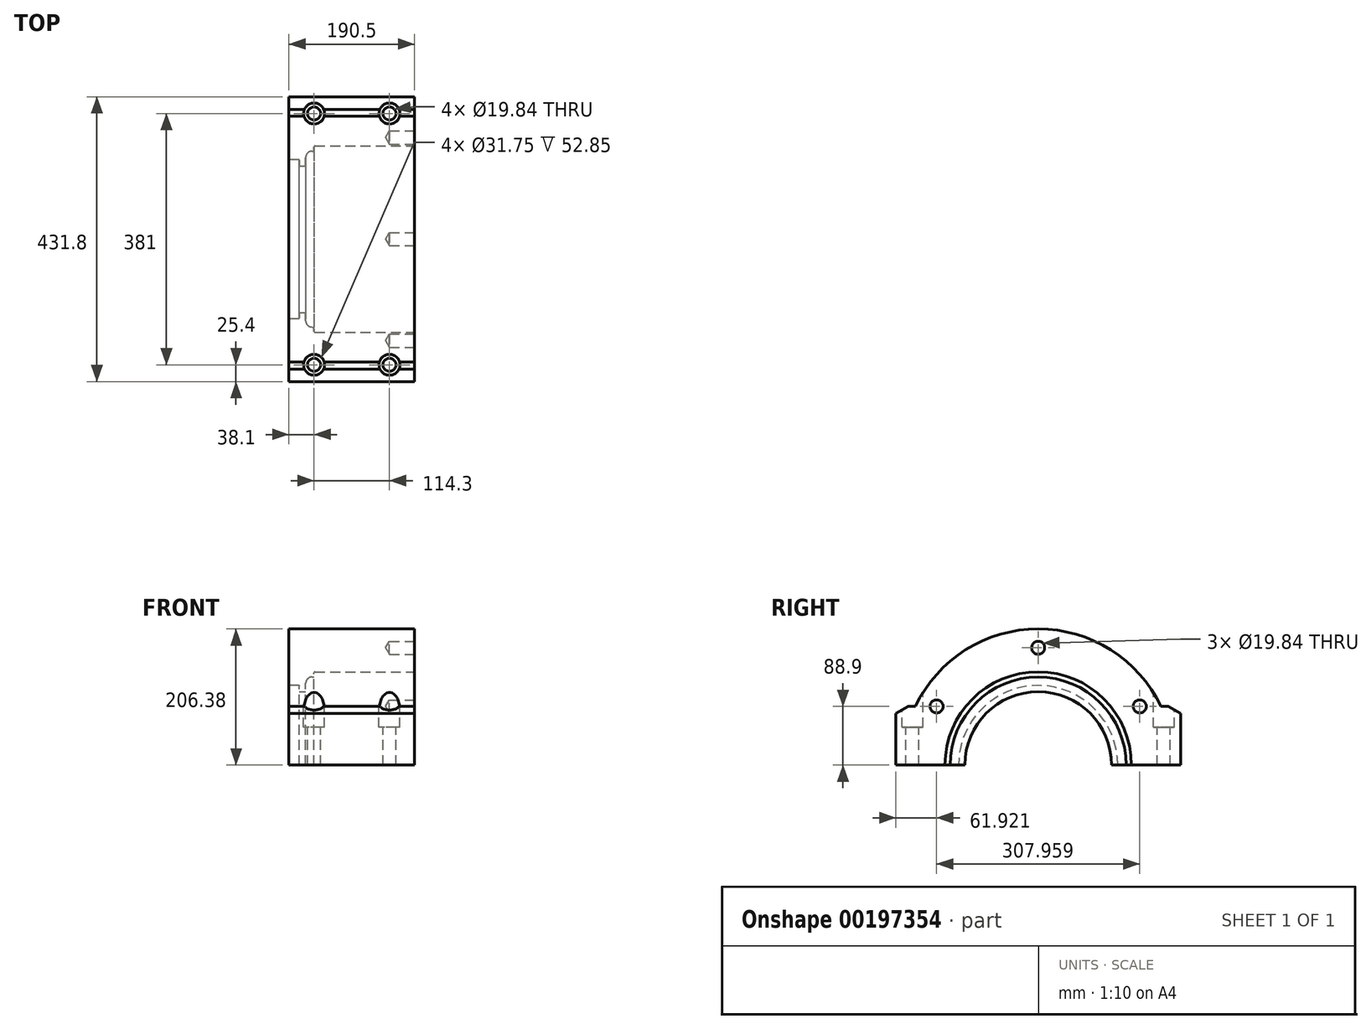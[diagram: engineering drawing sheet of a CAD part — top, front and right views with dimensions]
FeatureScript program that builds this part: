
annotation { "Feature Type Name" : "Feature", "Feature Type Description" : "" }
export const myFeature = defineFeature(function(context is Context, id is Id, definition is map)
    precondition{}
    {
        {
            var Q0;
            Q0=qCreatedBy(makeId("Right.planeOp"),FACE);
            var sketch = newSketch(context, id + "F0", { "sketchPlane" : qUnion([Q0])});
            skArc(sketch, "E0", {"start": v(186.25, 88.9) * mm, "mid": v(0, 206.38) * mm, "end": v(-186.25, 88.9) * mm});
            skLineSegment(sketch, "E1", {"start": v(-206.38, 0) * mm, "end": v(206.38, 0) * mm});
            skLineSegment(sketch, "E2", {"start": v(0, 324.9) * mm, "end": v(0, -120.15) * mm, "construction": true});
            skLineSegment(sketch, "E3.0", {"start": v(-215.9, 324.9) * mm, "end": v(-215.9, 88.9) * mm, "construction": true});
            skLineSegment(sketch, "E4", {"start": v(-330.26, 0) * mm, "end": v(259.86, 0) * mm, "construction": true});
            skLineSegment(sketch, "E5.0", {"start": v(-330.26, 88.9) * mm, "end": v(-215.9, 88.9) * mm, "construction": true});
            skLineSegment(sketch, "E6.bottom", {"start": v(-196.85, 88.9) * mm, "end": v(-166.34, 88.9) * mm});
            skLineSegment(sketch, "E6.top", {"start": v(-215.9, 0) * mm, "end": v(-166.34, 0) * mm});
            skLineSegment(sketch, "E6.left", {"start": v(-215.9, 77.9) * mm, "end": v(-215.9, 0) * mm});
            skLineSegment(sketch, "E7.0", {"start": v(-196.85, 324.9) * mm, "end": v(-196.85, 88.9) * mm, "construction": true});
            skLineSegment(sketch, "E8", {"start": v(-196.85, 88.9) * mm, "end": v(-215.9, 77.9) * mm});
            skLineSegment(sketch, "E9.trimOffspring", {"start": v(-196.85, 88.9) * mm, "end": v(-186.25, 88.9) * mm, "construction": true});
            skLineSegment(sketch, "E10.trimOffspring", {"start": v(-215.9, 77.9) * mm, "end": v(-215.9, -120.15) * mm, "construction": true});
            skLineSegment(sketch, "E11.trimOffspring", {"start": v(-166.34, 88.9) * mm, "end": v(259.86, 88.9) * mm, "construction": true});
            skLineSegment(sketch, "E12.MirrorCS", {"start": v(196.85, 88.9) * mm, "end": v(215.9, 77.9) * mm});
            skLineSegment(sketch, "E13.MirrorCS", {"start": v(196.85, 88.9) * mm, "end": v(186.25, 88.9) * mm, "construction": true});
            skLineSegment(sketch, "E14.MirrorCS", {"start": v(196.85, 88.9) * mm, "end": v(166.34, 88.9) * mm});
            skLineSegment(sketch, "E15.MirrorCS", {"start": v(215.9, 77.9) * mm, "end": v(215.9, 0) * mm});
            skLineSegment(sketch, "E16.MirrorCS", {"start": v(215.9, 0) * mm, "end": v(166.34, 0) * mm});
            skLineSegment(sketch, "E17.trimOffspring", {"start": v(-196.85, 0) * mm, "end": v(-196.85, -120.15) * mm, "construction": true});
            skSolve(sketch);
        }
        {
            var Q0;
            Q0 = qSketchRegion(id + "F0", true);
            extrude(context, id + "F1", {"entities" : qUnion([Q0]), "depth" : 190.5 * mm});
        }
        {
            var Q0;
            Q0=makeQuery(id+"F1.opExtrude","CAP_FACE",FACE,{"disambiguationData":[OSD([sQuery(id+"F0.wireOp",EDGE,"E0"),sQuery(id+"F0.wireOp",EDGE,"E1"),sQuery(id+"F0.wireOp",EDGE,"E6.bottom"),sQuery(id+"F0.wireOp",EDGE,"E6.top"),sQuery(id+"F0.wireOp",EDGE,"E6.left"),sQuery(id+"F0.wireOp",EDGE,"E8"),sQuery(id+"F0.wireOp",EDGE,"E12.MirrorCS"),sQuery(id+"F0.wireOp",EDGE,"E14.MirrorCS"),sQuery(id+"F0.wireOp",EDGE,"E15.MirrorCS"),sQuery(id+"F0.wireOp",EDGE,"E16.MirrorCS")])],"isStart":false});
            var sketch = newSketch(context, id + "F2", { "sketchPlane" : qUnion([Q0])});
            skCircle(sketch, "E18", {"center": v(0, 0) * mm, "radius": 141.29 * mm});
            skSolve(sketch);
        }
        {
            var Q0;
            Q0 = qSketchRegion(id + "F2", true);
            extrude(context, id + "F3", {"entities" : qUnion([Q0]), "operationType" : NewBodyOperationType.REMOVE, "oppositeDirection" : true, "depth" : 152.4 * mm});
        }
        {
            var Q0;
            Q0=makeQuery(id+"F3.boolean.opBoolean","COPY",FACE,{"derivedFrom":makeQuery(id+"F3.opExtrude","CAP_FACE",FACE,{"disambiguationData":[OSD([sQuery(id+"F2.wireOp",EDGE,"E18")])],"isStart":false})});
            var sketch = newSketch(context, id + "F4", { "sketchPlane" : qUnion([Q0])});
            skCircle(sketch, "E19", {"center": v(0, 0) * mm, "radius": 133.35 * mm});
            skSolve(sketch);
        }
        {
            var Q0;
            Q0 = qSketchRegion(id + "F4", true);
            extrude(context, id + "F5", {"entities" : qUnion([Q0]), "operationType" : NewBodyOperationType.REMOVE, "oppositeDirection" : true, "depth" : 12.7 * mm});
        }
        {
            var Q0;
            Q0=makeQuery(id+"F5.boolean.opBoolean","COPY",FACE,{"derivedFrom":makeQuery(id+"F5.opExtrude","CAP_FACE",FACE,{"disambiguationData":[OSD([sQuery(id+"F4.wireOp",EDGE,"E19")])],"isStart":false})});
            var sketch = newSketch(context, id + "F6", { "sketchPlane" : qUnion([Q0])});
            skCircle(sketch, "E20", {"center": v(0, 0) * mm, "radius": 111.13 * mm});
            skSolve(sketch);
        }
        {
            var Q0;
            Q0 = qSketchRegion(id + "F6", true);
            extrude(context, id + "F7", {"entities" : qUnion([Q0]), "operationType" : NewBodyOperationType.REMOVE, "endBound" : BoundingType.THROUGH_ALL, "oppositeDirection" : true, "depth" : 25.4 * mm});
        }
        {
            var Q0;
            Q0=makeQuery(id+"F3.boolean.opBoolean","COPY",EDGE,{"derivedFrom":makeQuery(id+"F3.opExtrude","CAP_EDGE",EDGE,{"disambiguationData":[OSD([sQuery(id+"F2.wireOp",EDGE,"E18")])],"isStart":false})});
            fillet(context, id + "F8", {"entities" : qUnion([Q0]), "radius" : 1.52 * mm, "tangentPropagation" : true, "allowEdgeOverflow" : false});
        }
        {
            var Q0;
            Q0=makeQuery(id+"F5.boolean.opBoolean","COPY",EDGE,{"derivedFrom":makeQuery(id+"F5.opExtrude","CAP_EDGE",EDGE,{"disambiguationData":[OSD([sQuery(id+"F4.wireOp",EDGE,"E19")])],"isStart":false})});
            fillet(context, id + "F9", {"entities" : qUnion([Q0]), "radius" : 9.65 * mm, "tangentPropagation" : true, "allowEdgeOverflow" : false});
        }
        {
            var Q0;
            Q0=makeQuery(id+"F1.opExtrude","CAP_FACE",FACE,{"disambiguationData":[OSD([sQuery(id+"F0.wireOp",EDGE,"E0"),sQuery(id+"F0.wireOp",EDGE,"E1"),sQuery(id+"F0.wireOp",EDGE,"E6.bottom"),sQuery(id+"F0.wireOp",EDGE,"E6.top"),sQuery(id+"F0.wireOp",EDGE,"E6.left"),sQuery(id+"F0.wireOp",EDGE,"E8"),sQuery(id+"F0.wireOp",EDGE,"E12.MirrorCS"),sQuery(id+"F0.wireOp",EDGE,"E14.MirrorCS"),sQuery(id+"F0.wireOp",EDGE,"E15.MirrorCS"),sQuery(id+"F0.wireOp",EDGE,"E16.MirrorCS")])],"isStart":true});
            var sketch = newSketch(context, id + "F10", { "sketchPlane" : qUnion([Q0])});
            skCircle(sketch, "E21", {"center": v(0, 0) * mm, "radius": 120.65 * mm});
            skSolve(sketch);
        }
        {
            var Q0;
            Q0 = qSketchRegion(id + "F10", true);
            extrude(context, id + "F11", {"entities" : qUnion([Q0]), "operationType" : NewBodyOperationType.REMOVE, "oppositeDirection" : true, "depth" : 15.75 * mm});
        }
        {
            var Q0;
            Q0=makeQuery(id+"F11.boolean.opBoolean","COPY",EDGE,{"derivedFrom":makeQuery(id+"F11.opExtrude","CAP_EDGE",EDGE,{"disambiguationData":[OSD([sQuery(id+"F10.wireOp",EDGE,"E21")])],"isStart":false})});
            fillet(context, id + "F12", {"entities" : qUnion([Q0]), "radius" : 0.76 * mm, "tangentPropagation" : true, "allowEdgeOverflow" : false});
        }
        {
            var Q0;
            Q0=makeQuery(id+"F1.opExtrude","CAP_FACE",FACE,{"disambiguationData":[OSD([sQuery(id+"F0.wireOp",EDGE,"E0"),sQuery(id+"F0.wireOp",EDGE,"E1"),sQuery(id+"F0.wireOp",EDGE,"E6.bottom"),sQuery(id+"F0.wireOp",EDGE,"E6.top"),sQuery(id+"F0.wireOp",EDGE,"E6.left"),sQuery(id+"F0.wireOp",EDGE,"E8"),sQuery(id+"F0.wireOp",EDGE,"E12.MirrorCS"),sQuery(id+"F0.wireOp",EDGE,"E14.MirrorCS"),sQuery(id+"F0.wireOp",EDGE,"E15.MirrorCS"),sQuery(id+"F0.wireOp",EDGE,"E16.MirrorCS")])],"isStart":false});
            var sketch = newSketch(context, id + "F13", { "sketchPlane" : qUnion([Q0])});
            skCircle(sketch, "E22", {"center": v(0, 0) * mm, "radius": 177.8 * mm, "construction": true});
            skLineSegment(sketch, "E23", {"start": v(0, 0) * mm, "end": v(0, 258.36) * mm, "construction": true});
            skPoint(sketch, "E23.endSnap0", {"position": v(0, 206.38) * mm});
            skPoint(sketch, "E24", {"position": v(0, 177.8) * mm});
            skPoint(sketch, "E25.1.0", {"position": v(-153.98, 88.9) * mm});
            skPoint(sketch, "E25.2.0", {"position": v(-153.98, -88.9) * mm});
            skPoint(sketch, "E25.3.0", {"position": v(0, -177.8) * mm});
            skPoint(sketch, "E25.4.0", {"position": v(153.98, -88.9) * mm});
            skPoint(sketch, "E25.5.0", {"position": v(153.98, 88.9) * mm});
            skSolve(sketch);
        }
        {
            var Q0;
            Q0=sQuery(id+"F13.wireOp",VERTEX,"E25.1.0");
            var Q1;
            Q1=sQuery(id+"F13.wireOp",VERTEX,"E24");
            var Q2;
            Q2=sQuery(id+"F13.wireOp",VERTEX,"E25.5.0");
            var Q3;
            Q3=makeQuery(id+"F1.opExtrude","SWEPT_BODY",BODY,{"disambiguationData":[OSD([sQuery(id+"F0.wireOp",EDGE,"E0"),sQuery(id+"F0.wireOp",EDGE,"E1"),sQuery(id+"F0.wireOp",EDGE,"E6.bottom"),sQuery(id+"F0.wireOp",EDGE,"E6.top"),sQuery(id+"F0.wireOp",EDGE,"E6.left"),sQuery(id+"F0.wireOp",EDGE,"E8"),sQuery(id+"F0.wireOp",EDGE,"E12.MirrorCS"),sQuery(id+"F0.wireOp",EDGE,"E14.MirrorCS"),sQuery(id+"F0.wireOp",EDGE,"E15.MirrorCS"),sQuery(id+"F0.wireOp",EDGE,"E16.MirrorCS")])]});
            hole(context, id + "F14", {"style" : HoleStyle.SIMPLE, "endStyle" : HoleEndStyle.BLIND, "standardTappedOrClearance" : lookupTablePath({ "standard" : "ANSI", "fit" : "Normal (ASME)", "size" : "3/4", "type" : "Clearance" }), "standardBlindInLast" : lookupTablePath({ "fit" : "Free", "standard" : "ANSI", "size" : "3/4", "type" : "Clearance" }), "holeDiameter" : 19.84 * mm, "holeDepth" : 38.1 * mm, "locations" : qUnion([Q0, Q1, Q2]), "scope" : qUnion([Q3])});
        }
        {
            var Q0;
            Q0=makeQuery(id+"F1.opExtrude","SWEPT_FACE",FACE,{"disambiguationData":[OSD([sQuery(id+"F0.wireOp",EDGE,"E6.bottom")])]});
            var sketch = newSketch(context, id + "F15", { "sketchPlane" : qUnion([Q0])});
            skLineSegment(sketch, "E26", {"start": v(-111.46, 0) * mm, "end": v(308.18, 0) * mm, "construction": true});
            skLineSegment(sketch, "E27.0", {"start": v(190.5, 186.25) * mm, "end": v(190.5, -190.5) * mm, "construction": true});
            skLineSegment(sketch, "E28.0", {"start": v(-111.46, -190.5) * mm, "end": v(308.18, -190.5) * mm, "construction": true});
            skPoint(sketch, "E29.orphan", {"position": v(190.5, -186.25) * mm});
            skLineSegment(sketch, "E30.0", {"start": v(152.4, 186.25) * mm, "end": v(152.4, -190.5) * mm, "construction": true});
            skLineSegment(sketch, "E31.2", {"start": v(196.85, -192.6) * mm, "end": v(196.85, -190.5) * mm, "construction": true});
            skLineSegment(sketch, "E32.trimOffspring", {"start": v(-6.35, -190.5) * mm, "end": v(-6.35, -192.6) * mm, "construction": true});
            skLineSegment(sketch, "E33.0", {"start": v(38.1, 186.25) * mm, "end": v(38.1, -190.5) * mm, "construction": true});
            skPoint(sketch, "E34", {"position": v(152.4, -190.5) * mm});
            skPoint(sketch, "E35", {"position": v(38.1, -190.5) * mm});
            skPoint(sketch, "E36.MirrorP", {"position": v(38.1, 190.5) * mm});
            skPoint(sketch, "E37.MirrorP", {"position": v(152.4, 190.5) * mm});
            skSolve(sketch);
        }
        {
            var Q0;
            Q0=sQuery(id+"F15.wireOp",VERTEX,"E35");
            var Q1;
            Q1=sQuery(id+"F15.wireOp",VERTEX,"E34");
            var Q2;
            Q2=sQuery(id+"F15.wireOp",VERTEX,"E36.MirrorP");
            var Q3;
            Q3=sQuery(id+"F15.wireOp",VERTEX,"E37.MirrorP");
            var Q4;
            Q4=makeQuery(id+"F1.opExtrude","SWEPT_BODY",BODY,{"disambiguationData":[OSD([sQuery(id+"F0.wireOp",EDGE,"E0"),sQuery(id+"F0.wireOp",EDGE,"E1"),sQuery(id+"F0.wireOp",EDGE,"E6.bottom"),sQuery(id+"F0.wireOp",EDGE,"E6.top"),sQuery(id+"F0.wireOp",EDGE,"E6.left"),sQuery(id+"F0.wireOp",EDGE,"E8"),sQuery(id+"F0.wireOp",EDGE,"E12.MirrorCS"),sQuery(id+"F0.wireOp",EDGE,"E14.MirrorCS"),sQuery(id+"F0.wireOp",EDGE,"E15.MirrorCS"),sQuery(id+"F0.wireOp",EDGE,"E16.MirrorCS")])]});
            hole(context, id + "F16", {"style" : HoleStyle.C_BORE, "endStyle" : HoleEndStyle.THROUGH, "holeDiameter" : 19.84 * mm, "cBoreDiameter" : 31.75 * mm, "cBoreDepth" : 31.75 * mm, "locations" : qUnion([Q0, Q1, Q2, Q3]), "scope" : qUnion([Q4]), "isTappedThrough" : true});
        }
        {
            var Q0;
            {var subQ1=makeQuery(id+"F16.hole-0.opRevolve","SWEPT_FACE",FACE,{"disambiguationData":[OSD([sQuery(id+"F16.hole-0.sketch.wireOp",EDGE,"cbore_start_line_2")])]});var subQ2=sQuery(id+"F0.wireOp",EDGE,"E8");var subQ4=sQuery(id+"F0.wireOp",EDGE,"E0");var subQ6=sQuery(id+"F0.wireOp",EDGE,"E6.bottom");Q0=makeQuery(id+"F16.hole-1.boolean.opBoolean","SPLIT",FACE,{"disambiguationData":[TD([makeQuery(id+"F16.hole-0.boolean.opBoolean","COPY",FACE,{"derivedFrom":subQ1})])],"derivedFrom":makeQuery(id+"F16.hole-0.boolean.opBoolean","SPLIT",FACE,{"disambiguationData":[TD([makeQuery(id+"F1.opExtrude","CAP_FACE",FACE,{"disambiguationData":[OSD([subQ4,sQuery(id+"F0.wireOp",EDGE,"E1"),subQ6,sQuery(id+"F0.wireOp",EDGE,"E6.top"),sQuery(id+"F0.wireOp",EDGE,"E6.left"),subQ2,sQuery(id+"F0.wireOp",EDGE,"E12.MirrorCS"),sQuery(id+"F0.wireOp",EDGE,"E14.MirrorCS"),sQuery(id+"F0.wireOp",EDGE,"E15.MirrorCS"),sQuery(id+"F0.wireOp",EDGE,"E16.MirrorCS")])],"isStart":false})])],"derivedFrom":makeQuery(id+"F1.opExtrude","SWEPT_FACE",FACE,{"disambiguationData":[OSD([subQ6])]})})});}
            var sketch = newSketch(context, id + "F17", { "sketchPlane" : qUnion([Q0])});
            skCircle(sketch, "E38.0", {"center": v(38.1, -190.5) * mm, "radius": 15.88 * mm});
            skCircle(sketch, "E39.0", {"center": v(152.4, -190.5) * mm, "radius": 15.88 * mm});
            skCircle(sketch, "E40.0", {"center": v(38.1, 190.5) * mm, "radius": 15.88 * mm});
            skCircle(sketch, "E41.0", {"center": v(152.4, 190.5) * mm, "radius": 15.88 * mm});
            skSolve(sketch);
        }
        {
            var Q0;
            Q0 = qSketchRegion(id + "F17", true);
            extrude(context, id + "F18", {"entities" : qUnion([Q0]), "operationType" : NewBodyOperationType.REMOVE, "endBound" : BoundingType.THROUGH_ALL, "depth" : 25.4 * mm});
        }
    });
